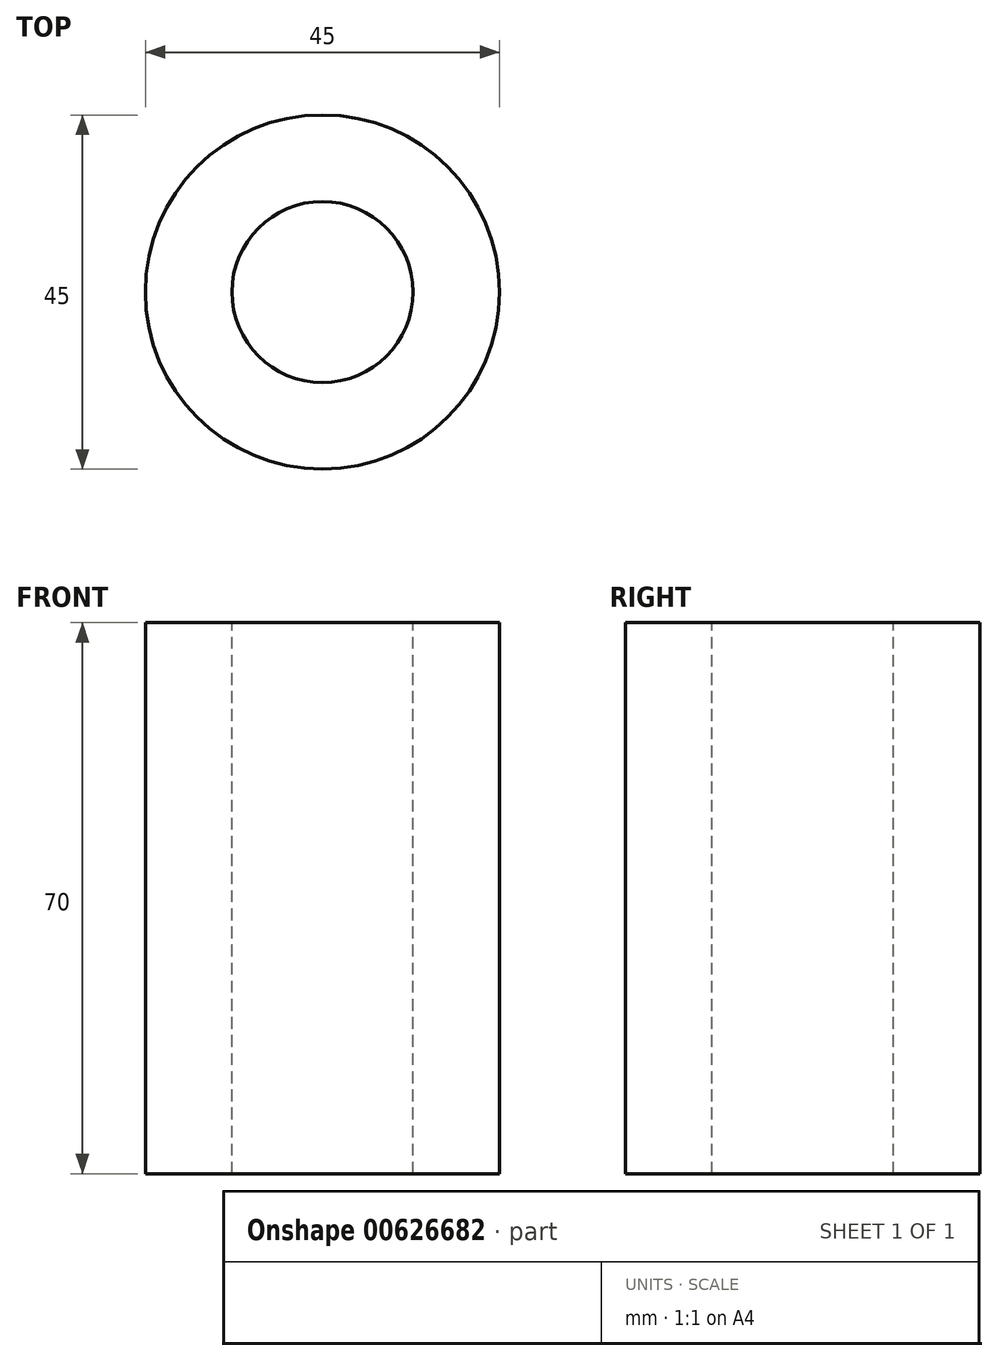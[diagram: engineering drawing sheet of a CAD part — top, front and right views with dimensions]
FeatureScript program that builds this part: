
annotation { "Feature Type Name" : "Feature", "Feature Type Description" : "" }
export const myFeature = defineFeature(function(context is Context, id is Id, definition is map)
    precondition{}
    {
        {
            var Q0;
            Q0=qCreatedBy(makeId("Top.planeOp"),FACE);
            var sketch = newSketch(context, id + "F0", { "sketchPlane" : qUnion([Q0])});
            skCircle(sketch, "E0", {"center": v(-41.54, 17.62) * mm, "radius": 22.5 * mm});
            skSolve(sketch);
        }
        {
            var Q0;
            Q0 = qSketchRegion(id + "F0", true);
            extrude(context, id + "F1", {"entities" : qUnion([Q0]), "depth" : 70 * mm, "offsetDistance" : 25 * mm});
        }
        {
            var Q0;
            Q0=makeQuery(id+"F1.opExtrude","CAP_FACE",FACE,{"disambiguationData":[OSD([sQuery(id+"F0.wireOp",EDGE,"E0")])],"isStart":false});
            var sketch = newSketch(context, id + "F2", { "sketchPlane" : qUnion([Q0])});
            skCircle(sketch, "E1", {"center": v(-41.54, 17.62) * mm, "radius": 11.5 * mm});
            skSolve(sketch);
        }
        {
            var Q0;
            Q0 = qSketchRegion(id + "F2", true);
            extrude(context, id + "F3", {"entities" : qUnion([Q0]), "operationType" : NewBodyOperationType.REMOVE, "oppositeDirection" : true, "depth" : 84.1 * mm, "offsetDistance" : 25 * mm});
        }
        {
            var Q0;
            Q0=qCreatedBy(makeId("Front.planeOp"),FACE);
            cPlane(context, id + "F4", {"entities" : qUnion([Q0]), "cplaneType" : CPlaneType.OFFSET, "offset" : 7 * mm, "width" : 150 * mm, "height" : 150 * mm});
        }
    });
